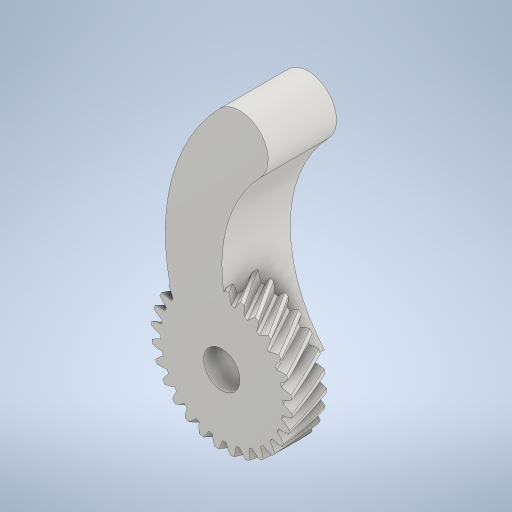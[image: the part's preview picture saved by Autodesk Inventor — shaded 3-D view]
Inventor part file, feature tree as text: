
AUTODESK INVENTOR PART (.ipt)
format: ipt  version: 2024 (Build 280153000, 153)  size: 1,498,112 bytes
history: native  units: mm (DEFAULTED — no unit token found)
features: extrude x3, plane x3, other x3, sketch x3, projected_geometry x1
ambient origin geometry x8: Origin, YZ Plane, XZ Plane, XY Plane, X Axis, Y Axis, Z Axis, Center Point
bodies: Solid1 (feature_tree)
feature tree (13):
  extrude  "Extrusion1"  Depth=5.0mm TaperAngle=0.0deg
  plane  "Work Plane2"
  plane  "Work Plane8"
  plane  "Work Plane9"
  other  "Spur Gear"
  extrude  "Extrusion2"  Depth=10.0mm TaperAngle=0.0deg
  extrude  "Extrusion3"  Depth=10.0mm TaperAngle=0.0deg
  sketch  "Sketch1"  dims[d0=20.587946mm d1=5.0mm d2=0.0mm]
  other  "Srf1"
  sketch  "Sketch3"  dims[d3=19.398969mm d4=10.0mm d5=0.0mm]
  sketch  "Sketch4"  dims[d16=20.0mm d17=0.0mm d34=1.121997mm d39=0.0mm d41=0.0mm d43=20.0mm d46=20.0mm d47=0.0mm d48=0.0mm d49=5.3mm d50=10.0mm d51=0.0mm d52=5.0mm d53=5.0mm d54=40.0mm d55=20.0mm d58=56.568542mm d59=30.0mm d60=10.0mm d61=0.0mm]
  projected_geometry  "Projected Loop1"
  other  "Pitch Diameter"
